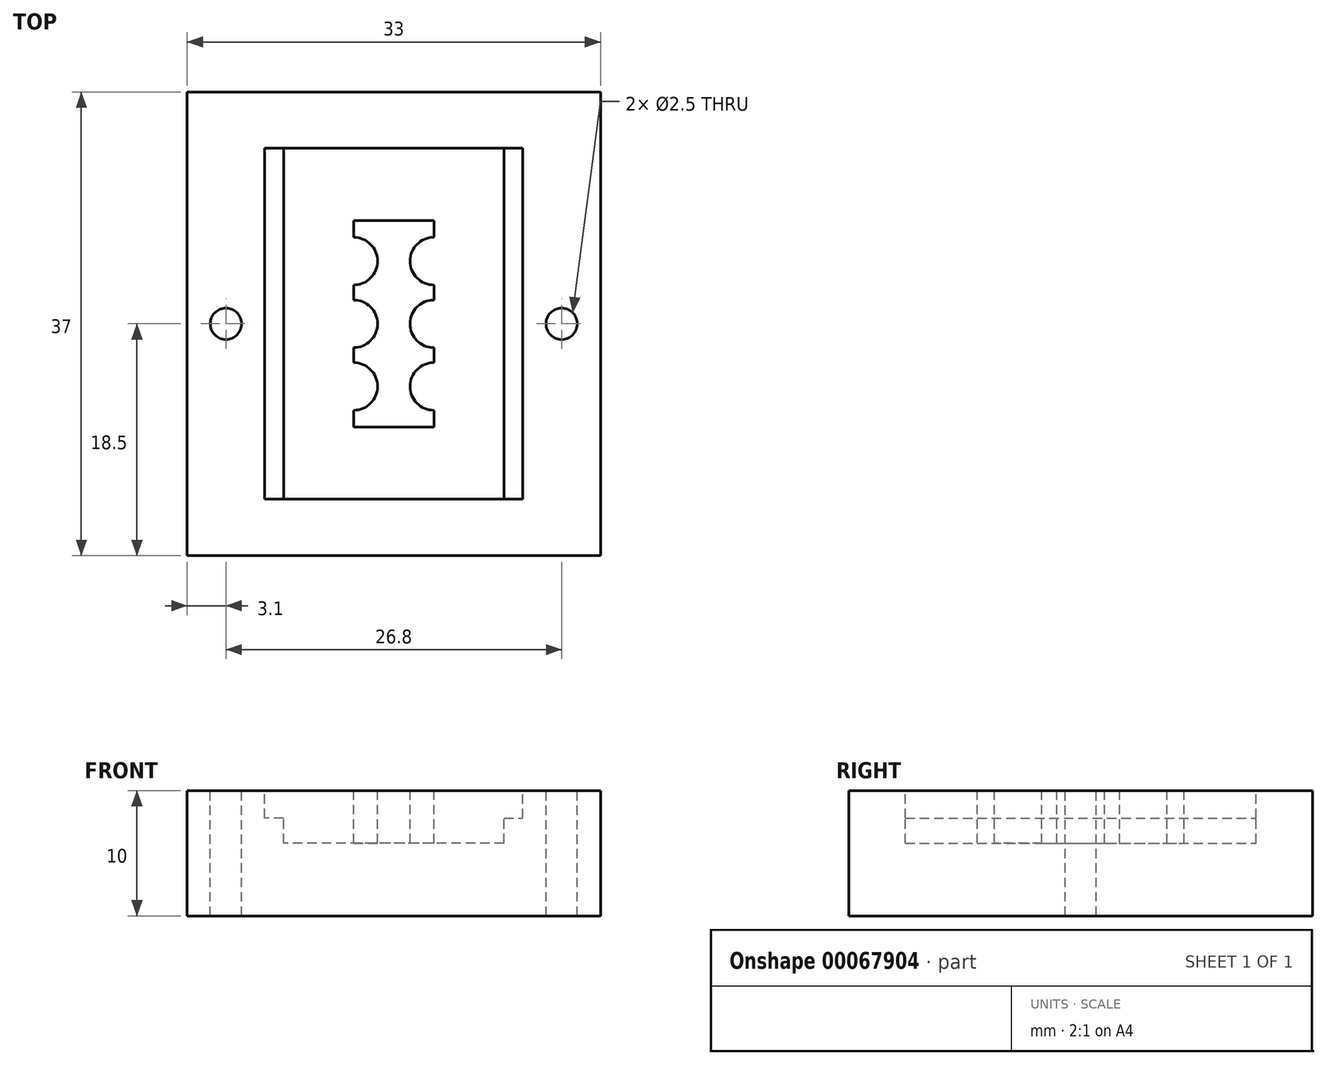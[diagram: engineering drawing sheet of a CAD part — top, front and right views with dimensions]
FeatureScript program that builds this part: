
annotation { "Feature Type Name" : "Feature", "Feature Type Description" : "" }
export const myFeature = defineFeature(function(context is Context, id is Id, definition is map)
    precondition{}
    {
        {
            var Q0;
            Q0=qCreatedBy(makeId("Top.planeOp"),FACE);
            var sketch = newSketch(context, id + "F0", { "sketchPlane" : qUnion([Q0])});
            skLineSegment(sketch, "E0.rect.bottom", {"start": v(16.5, -18.5) * mm, "end": v(-16.5, -18.5) * mm});
            skLineSegment(sketch, "E0.rect.top", {"start": v(16.5, 18.5) * mm, "end": v(-16.5, 18.5) * mm});
            skLineSegment(sketch, "E0.rect.left", {"start": v(16.5, -18.5) * mm, "end": v(16.5, 18.5) * mm});
            skLineSegment(sketch, "E0.rect.right", {"start": v(-16.5, -18.5) * mm, "end": v(-16.5, 18.5) * mm});
            skPoint(sketch, "E0.rect.middle", {"position": v(0, 0) * mm});
            skSolve(sketch);
        }
        {
            var Q0;
            Q0 = qSketchRegion(id + "F0", true);
            extrude(context, id + "F1", {"entities" : qUnion([Q0]), "depth" : 10 * mm});
        }
        {
            var Q0;
            Q0=makeQuery(id+"F1.opExtrude","CAP_FACE",FACE,{"disambiguationData":[OSD([sQuery(id+"F0.wireOp",EDGE,"E0.rect.bottom"),sQuery(id+"F0.wireOp",EDGE,"E0.rect.top"),sQuery(id+"F0.wireOp",EDGE,"E0.rect.left"),sQuery(id+"F0.wireOp",EDGE,"E0.rect.right")])],"isStart":false});
            var sketch = newSketch(context, id + "F2", { "sketchPlane" : qUnion([Q0])});
            skLineSegment(sketch, "E1.rect.bottom", {"start": v(8.8, -14) * mm, "end": v(-8.8, -14) * mm});
            skLineSegment(sketch, "E1.rect.top", {"start": v(8.8, 14) * mm, "end": v(-8.8, 14) * mm});
            skLineSegment(sketch, "E1.rect.left", {"start": v(8.8, -14) * mm, "end": v(8.8, 14) * mm});
            skLineSegment(sketch, "E1.rect.right", {"start": v(-8.8, -14) * mm, "end": v(-8.8, 14) * mm});
            skPoint(sketch, "E1.rect.middle", {"position": v(0, 0) * mm});
            skLineSegment(sketch, "E2.rect.bottom", {"start": v(3.2, -8.25) * mm, "end": v(-3.2, -8.25) * mm});
            skLineSegment(sketch, "E2.rect.top", {"start": v(3.2, 8.25) * mm, "end": v(-3.2, 8.25) * mm});
            skLineSegment(sketch, "E2.rect.left", {"start": v(3.2, -8.25) * mm, "end": v(3.2, -6.9) * mm});
            skLineSegment(sketch, "E2.rect.right", {"start": v(-3.2, -8.25) * mm, "end": v(-3.2, -6.9) * mm});
            skLineSegment(sketch, "E3", {"start": v(-17.9, 5) * mm, "end": v(21.1, 5) * mm, "construction": true});
            skLineSegment(sketch, "E4", {"start": v(-17.82, -5) * mm, "end": v(20.9, -5) * mm, "construction": true});
            skArc(sketch, "E5", {"start": v(-3.2, -1.9) * mm, "mid": v(-1.3, 0) * mm, "end": v(-3.2, 1.9) * mm});
            skArc(sketch, "E6", {"start": v(-3.2, 3.1) * mm, "mid": v(-1.3, 5) * mm, "end": v(-3.2, 6.9) * mm});
            skArc(sketch, "E7", {"start": v(-3.2, -6.9) * mm, "mid": v(-1.3, -5) * mm, "end": v(-3.2, -3.1) * mm});
            skArc(sketch, "E8", {"start": v(3.2, 6.9) * mm, "mid": v(1.3, 5) * mm, "end": v(3.2, 3.1) * mm});
            skArc(sketch, "E9", {"start": v(3.2, 1.9) * mm, "mid": v(1.3, 0) * mm, "end": v(3.2, -1.9) * mm});
            skArc(sketch, "E10", {"start": v(3.2, -3.1) * mm, "mid": v(1.3, -5) * mm, "end": v(3.2, -6.9) * mm});
            skLineSegment(sketch, "E11.trimOffspring", {"start": v(3.2, 6.9) * mm, "end": v(3.2, 8.25) * mm});
            skLineSegment(sketch, "E12.trimOffspring", {"start": v(-3.2, 6.9) * mm, "end": v(-3.2, 8.25) * mm});
            skLineSegment(sketch, "E13.trimOffspring", {"start": v(-3.2, 1.9) * mm, "end": v(-3.2, 3.1) * mm});
            skLineSegment(sketch, "E14.trimOffspring", {"start": v(-3.2, -3.1) * mm, "end": v(-3.2, -1.9) * mm});
            skLineSegment(sketch, "E15.trimOffspring", {"start": v(3.2, 1.9) * mm, "end": v(3.2, 3.1) * mm});
            skLineSegment(sketch, "E16.trimOffspring", {"start": v(3.2, -3.1) * mm, "end": v(3.2, -1.9) * mm});
            skSolve(sketch);
        }
        {
            var Q0;
            Q0 = qSketchRegion(id + "F2", true);
            extrude(context, id + "F3", {"entities" : qUnion([Q0]), "operationType" : NewBodyOperationType.REMOVE, "oppositeDirection" : true, "depth" : 4.2 * mm});
        }
        {
            var Q0;
            {var subQ0=sQuery(id+"F0.wireOp",EDGE,"E0.rect.right");var subQ1=sQuery(id+"F0.wireOp",EDGE,"E0.rect.left");var subQ2=sQuery(id+"F0.wireOp",EDGE,"E0.rect.top");var subQ3=sQuery(id+"F0.wireOp",EDGE,"E0.rect.bottom");Q0=makeQuery(id+"F3.boolean.opBoolean","SPLIT",FACE,{"disambiguationData":[TD([makeQuery(id+"F1.opExtrude","SWEPT_FACE",FACE,{"disambiguationData":[OSD([subQ3])]})])],"derivedFrom":makeQuery(id+"F1.opExtrude","CAP_FACE",FACE,{"disambiguationData":[OSD([subQ3,subQ2,subQ1,subQ0])],"isStart":false})});}
            var sketch = newSketch(context, id + "F4", { "sketchPlane" : qUnion([Q0])});
            skLineSegment(sketch, "E17.bottom", {"start": v(-8.8, 14) * mm, "end": v(-10.3, 14) * mm});
            skLineSegment(sketch, "E17.top", {"start": v(-8.8, -14) * mm, "end": v(-10.3, -14) * mm});
            skLineSegment(sketch, "E17.left", {"start": v(-8.8, 14) * mm, "end": v(-8.8, -14) * mm});
            skLineSegment(sketch, "E17.right", {"start": v(-10.3, 14) * mm, "end": v(-10.3, -14) * mm});
            skLineSegment(sketch, "E18.bottom", {"start": v(8.8, -14) * mm, "end": v(10.3, -14) * mm});
            skLineSegment(sketch, "E18.top", {"start": v(8.8, 14) * mm, "end": v(10.3, 14) * mm});
            skLineSegment(sketch, "E18.left", {"start": v(8.8, -14) * mm, "end": v(8.8, 14) * mm});
            skLineSegment(sketch, "E18.right", {"start": v(10.3, -14) * mm, "end": v(10.3, 14) * mm});
            skSolve(sketch);
        }
        {
            var Q0;
            Q0 = qSketchRegion(id + "F4", true);
            extrude(context, id + "F5", {"entities" : qUnion([Q0]), "operationType" : NewBodyOperationType.REMOVE, "oppositeDirection" : true, "depth" : 2.2 * mm});
        }
        {
            var Q0;
            {var subQ0=sQuery(id+"F0.wireOp",EDGE,"E0.rect.right");var subQ1=sQuery(id+"F0.wireOp",EDGE,"E0.rect.left");var subQ2=sQuery(id+"F0.wireOp",EDGE,"E0.rect.top");var subQ3=sQuery(id+"F0.wireOp",EDGE,"E0.rect.bottom");Q0=makeQuery(id+"F3.boolean.opBoolean","SPLIT",FACE,{"disambiguationData":[TD([makeQuery(id+"F1.opExtrude","SWEPT_FACE",FACE,{"disambiguationData":[OSD([subQ3])]})])],"derivedFrom":makeQuery(id+"F1.opExtrude","CAP_FACE",FACE,{"disambiguationData":[OSD([subQ3,subQ2,subQ1,subQ0])],"isStart":false})});}
            var sketch = newSketch(context, id + "F6", { "sketchPlane" : qUnion([Q0])});
            skCircle(sketch, "E19", {"center": v(13.4, 0) * mm, "radius": 1.25 * mm});
            skCircle(sketch, "E20", {"center": v(-13.4, 0) * mm, "radius": 1.25 * mm});
            skLineSegment(sketch, "E21.bottom", {"start": v(4, 14) * mm, "end": v(8.8, 14) * mm, "construction": true});
            skLineSegment(sketch, "E21.top", {"start": v(4, -14) * mm, "end": v(8.8, -14) * mm, "construction": true});
            skLineSegment(sketch, "E21.left", {"start": v(4, 14) * mm, "end": v(4, -14) * mm, "construction": true});
            skLineSegment(sketch, "E21.right", {"start": v(8.8, 14) * mm, "end": v(8.8, -14) * mm, "construction": true});
            skLineSegment(sketch, "E22.bottom", {"start": v(-8.8, 14) * mm, "end": v(-4, 14) * mm, "construction": true});
            skLineSegment(sketch, "E22.top", {"start": v(-8.8, -14) * mm, "end": v(-4, -14) * mm, "construction": true});
            skLineSegment(sketch, "E22.left", {"start": v(-8.8, 14) * mm, "end": v(-8.8, -14) * mm, "construction": true});
            skLineSegment(sketch, "E22.right", {"start": v(-4, 14) * mm, "end": v(-4, -14) * mm, "construction": true});
            skLineSegment(sketch, "E23", {"start": v(-6.4, 14) * mm, "end": v(-6.4, -14) * mm, "construction": true});
            skLineSegment(sketch, "E24", {"start": v(6.4, 14) * mm, "end": v(6.4, -14) * mm, "construction": true});
            skSolve(sketch);
        }
        {
            var Q0;
            Q0 = qSketchRegion(id + "F6", true);
            extrude(context, id + "F7", {"entities" : qUnion([Q0]), "operationType" : NewBodyOperationType.REMOVE, "endBound" : BoundingType.THROUGH_ALL, "oppositeDirection" : true, "depth" : 25 * mm});
        }
    });
